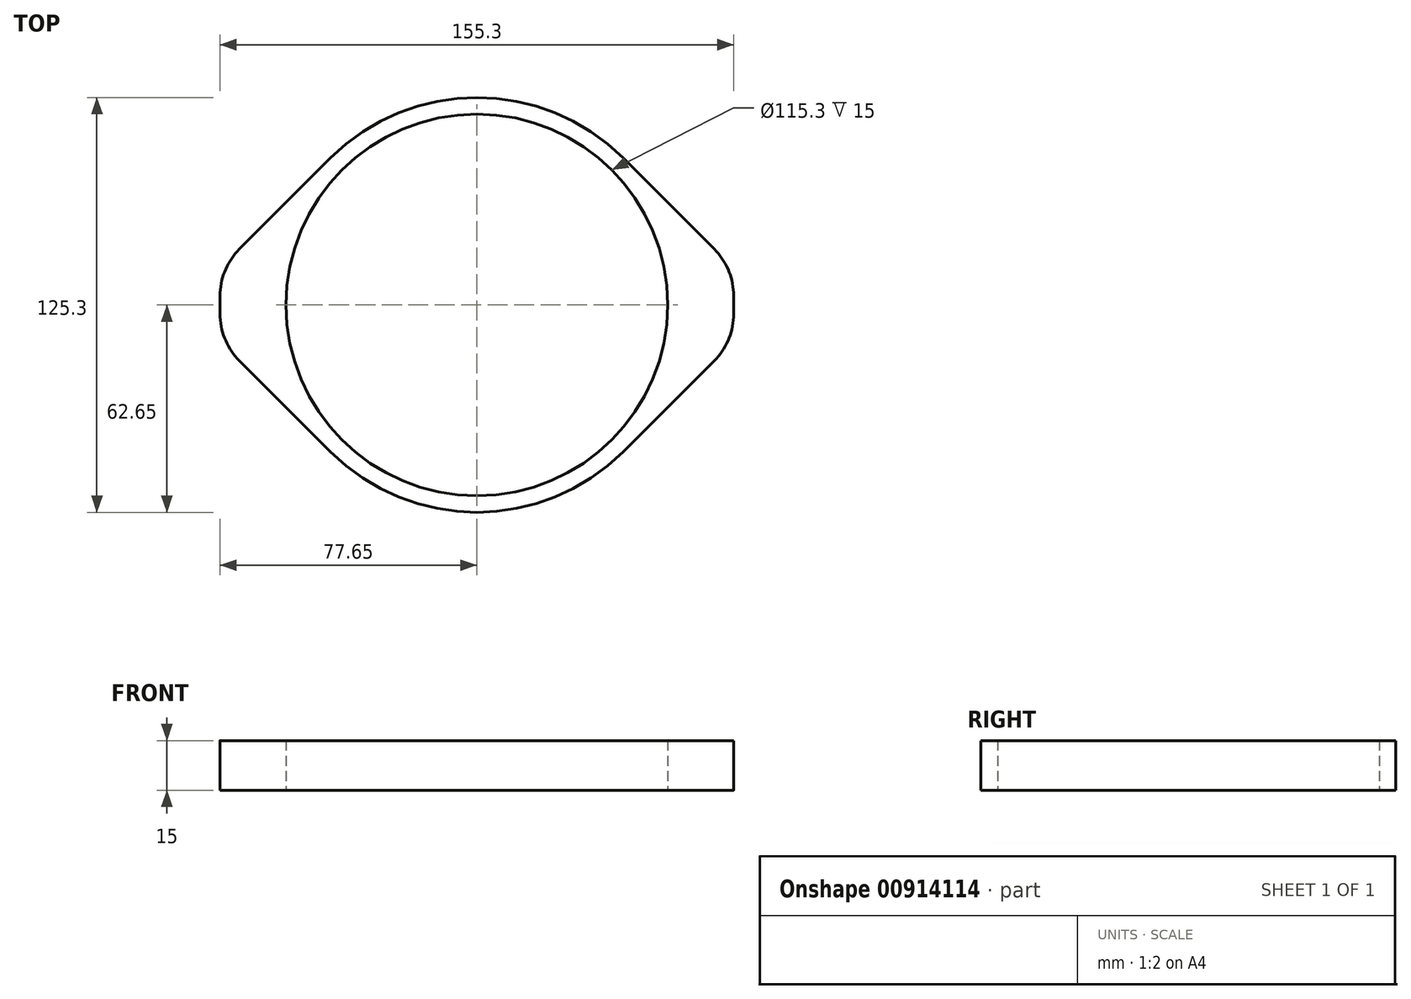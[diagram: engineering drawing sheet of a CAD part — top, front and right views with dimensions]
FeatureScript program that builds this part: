
annotation { "Feature Type Name" : "Feature", "Feature Type Description" : "" }
export const myFeature = defineFeature(function(context is Context, id is Id, definition is map)
    precondition{}
    {
        {
            var Q0;
            Q0=qCreatedBy(makeId("Top.planeOp"),FACE);
            var sketch = newSketch(context, id + "F0", { "sketchPlane" : qUnion([Q0])});
            skCircle(sketch, "E0", {"center": v(0, 0) * mm, "radius": 57.65 * mm});
            skArc(sketch, "E1.0", {"start": v(44.3, 44.3) * mm, "mid": v(0, 62.65) * mm, "end": v(-44.3, 44.3) * mm});
            skArc(sketch, "E2.0", {"start": v(-77.56, 3.68) * mm, "mid": v(-77.65, 0) * mm, "end": v(-77.56, -3.68) * mm});
            skArc(sketch, "E3.trimOffspring", {"start": v(77.56, -3.68) * mm, "mid": v(77.65, 0) * mm, "end": v(77.56, 3.68) * mm});
            skArc(sketch, "E4.trimOffspring", {"start": v(-44.3, -44.3) * mm, "mid": v(0, -62.65) * mm, "end": v(44.3, -44.3) * mm});
            skLineSegment(sketch, "E5", {"start": v(44.3, -44.3) * mm, "end": v(71.73, -16.87) * mm});
            skPoint(sketch, "E6.visualSharp", {"position": v(76.74, -11.86) * mm});
            skArc(sketch, "E6.filletArc", {"start": v(71.73, -16.87) * mm, "mid": v(75.88, -10.82) * mm, "end": v(77.56, -3.68) * mm});
            skLineSegment(sketch, "E7.MirrorCS", {"start": v(44.3, 44.3) * mm, "end": v(71.73, 16.87) * mm});
            skArc(sketch, "E8.MirrorCS", {"start": v(71.73, 16.87) * mm, "mid": v(75.88, 10.82) * mm, "end": v(77.56, 3.68) * mm});
            skLineSegment(sketch, "E9.MirrorCS", {"start": v(-44.3, -44.3) * mm, "end": v(-71.73, -16.87) * mm});
            skArc(sketch, "E10.MirrorCS", {"start": v(-71.73, -16.87) * mm, "mid": v(-75.88, -10.82) * mm, "end": v(-77.56, -3.68) * mm});
            skArc(sketch, "E11.MirrorCS", {"start": v(-71.73, 16.87) * mm, "mid": v(-75.88, 10.82) * mm, "end": v(-77.56, 3.68) * mm});
            skLineSegment(sketch, "E12.MirrorCS", {"start": v(-44.3, 44.3) * mm, "end": v(-71.73, 16.87) * mm});
            skSolve(sketch);
        }
        {
            var Q0;
            Q0=makeQuery(id+"F0.imprint","IMPRINT",FACE,{"disambiguationData":[TD([[makeQuery(id+"F0.imprint","IMPRINT",EDGE,{"derivedFrom":sQuery(id+"F0.wireOp",EDGE,"E0")}),-1.0]])]});
            extrude(context, id + "F1", {"entities" : qUnion([Q0]), "depth" : 15 * mm, "offsetDistance" : 25 * mm});
        }
    });
